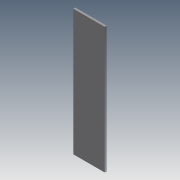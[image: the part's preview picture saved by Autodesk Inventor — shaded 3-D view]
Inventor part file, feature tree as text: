
AUTODESK INVENTOR PART (.ipt)
format: ipt  version: 2011 (Build 150239000, 239)  size: 132,608 bytes
history: native  units: in
note: dims shown in document units (in); Inventor stores cm internally (conversion verified against a paired STEP export)
features: extrude x10, sketch x10
ambient origin geometry x8: Origin, YZ Plane, XZ Plane, XY Plane, X Axis, Y Axis, Z Axis, Center Point
bodies: Solid1 (feature_tree)
feature tree (20):
  extrude  "Extrusion1"  Depth=12.0in
  extrude  "Extrusion2"  Depth=0.5in TaperAngle=0.0deg
  extrude  "Extrusion3"  Depth=1.5in TaperAngle=0.0deg
  extrude  "Extrusion4"  Depth=0.25in TaperAngle=0.0deg
  extrude  "Extrusion5"  Depth=0.5in TaperAngle=0.0deg
  extrude  "Extrusion6"  Depth=1.0in TaperAngle=0.0deg
  extrude  "Extrusion7"  Depth=1.0in TaperAngle=0.0deg
  extrude  "Extrusion8"  [1 undecoded]
  extrude  "Extrusion9"  [1 undecoded]
  extrude  "Extrusion10"  [1 undecoded]
  sketch  "Sketch1"  dims[d0=5.5in d1=12.0in]
  sketch  "Sketch2"  dims[d2=0.25in d3=0.0in d4=0.5in d5=0.0in]
  sketch  "Sketch3"  dims[d6=0.5in d7=0.0in d8=1.5in d9=0.0in]
  sketch  "Sketch4"  dims[d10=10.0in d11=0.25in d12=0.0in]
  sketch  "Sketch5"  dims[d13=5.0in d14=0.0in d15=0.5in d16=0.0in]
  sketch  "Sketch6"  dims[d17=0.75in d18=1.0in d19=0.0in]
  sketch  "Sketch7"  dims[d20=0.25in d21=1.0in d22=0.0in]
  sketch  "Sketch8"  dims[d23=0.5in d24=0.0in]
  sketch  "Sketch9"
  sketch  "Sketch10"
note: 3 required parameter values undecoded (feature->parameter linkage not recoverable at this tier; creation-order binding heuristic only, values carry confidence <= 0.55)
